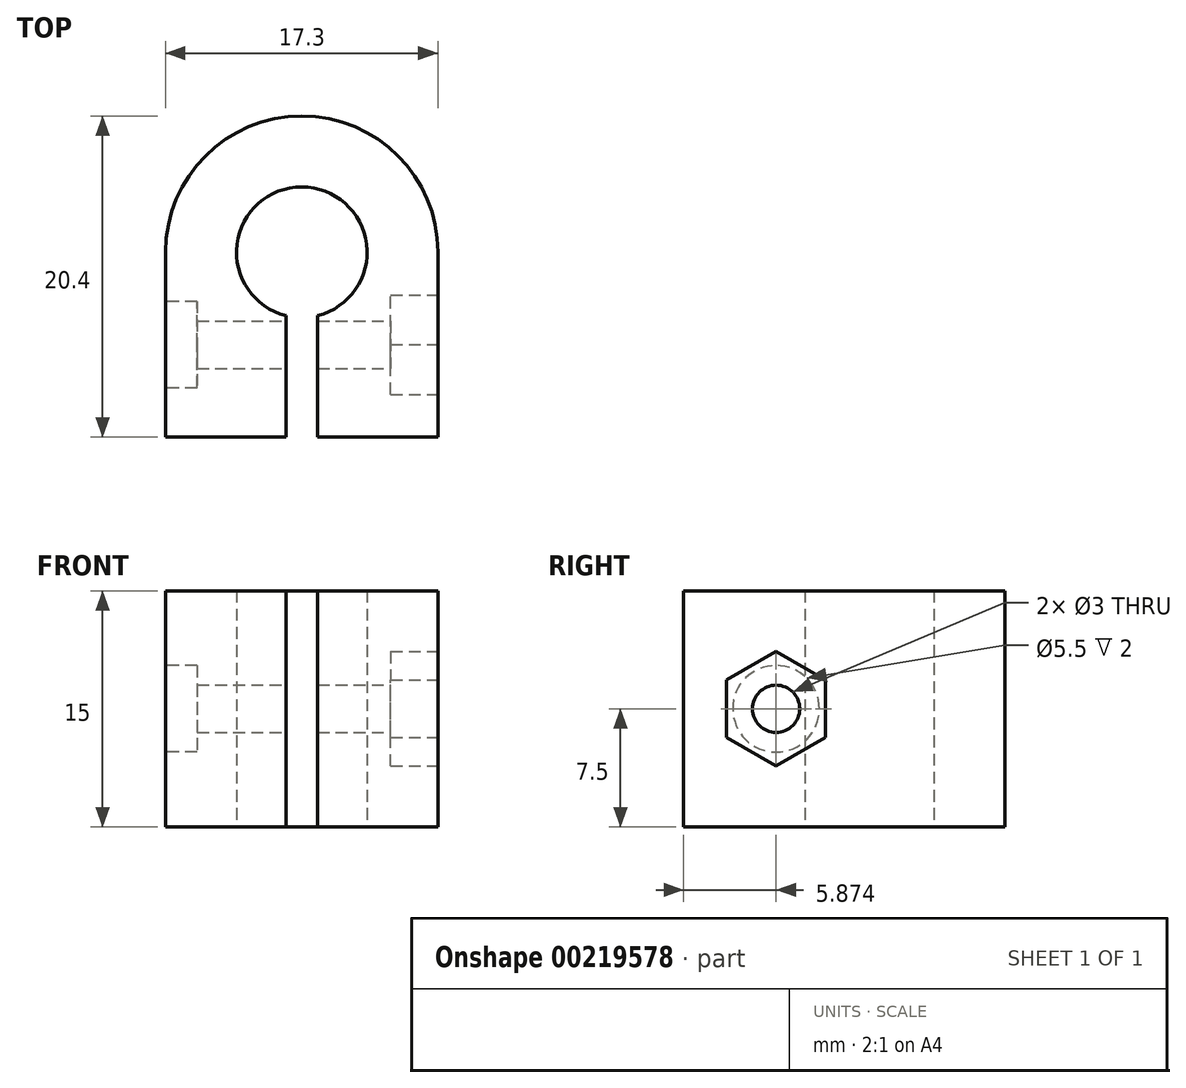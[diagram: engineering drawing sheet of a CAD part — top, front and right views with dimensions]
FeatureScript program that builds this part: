
annotation { "Feature Type Name" : "Feature", "Feature Type Description" : "" }
export const myFeature = defineFeature(function(context is Context, id is Id, definition is map)
    precondition{}
    {
        {
            var Q0;
            Q0=qCreatedBy(makeId("Top.planeOp"),FACE);
            var sketch = newSketch(context, id + "F0", { "sketchPlane" : qUnion([Q0])});
            skCircle(sketch, "E0", {"center": v(0, 0) * mm, "radius": 4.15 * mm});
            skCircle(sketch, "E1", {"center": v(0, 0) * mm, "radius": 8.65 * mm});
            skLineSegment(sketch, "E2.bottom", {"start": v(-8.65, -11.75) * mm, "end": v(8.65, -11.75) * mm});
            skLineSegment(sketch, "E2.top", {"start": v(-8.65, 0) * mm, "end": v(8.65, 0) * mm});
            skLineSegment(sketch, "E2.left", {"start": v(-8.65, -11.75) * mm, "end": v(-8.65, 0) * mm});
            skLineSegment(sketch, "E2.right", {"start": v(8.65, -11.75) * mm, "end": v(8.65, 0) * mm});
            skLineSegment(sketch, "E3.bottom", {"start": v(1, -4.03) * mm, "end": v(-1, -4.03) * mm});
            skLineSegment(sketch, "E3.top", {"start": v(1, -11.75) * mm, "end": v(-1, -11.75) * mm});
            skLineSegment(sketch, "E3.left", {"start": v(1, -4.03) * mm, "end": v(1, -11.75) * mm});
            skLineSegment(sketch, "E3.right", {"start": v(-1, -4.03) * mm, "end": v(-1, -11.75) * mm});
            skPoint(sketch, "E3.middle", {"position": v(0, -7.89) * mm});
            skSolve(sketch);
        }
        {
            var Q0;
            {var subQ0=sQuery(id+"F0.wireOp",EDGE,"E2.left");Q0=makeQuery(id+"F0.imprint","IMPRINT",FACE,{"disambiguationData":[TD([[makeQuery(id+"F0.imprint","IMPRINT",EDGE,{"derivedFrom":subQ0}),-1.0]])]});}
            var Q1;
            {var subQ0=sQuery(id+"F0.wireOp",EDGE,"E2.right");Q1=makeQuery(id+"F0.imprint","IMPRINT",FACE,{"disambiguationData":[TD([[makeQuery(id+"F0.imprint","IMPRINT",EDGE,{"derivedFrom":subQ0}),1.0]])]});}
            var Q2;
            {var subQ0=sQuery(id+"F0.wireOp",EDGE,"E2.top");var subQ1=sQuery(id+"F0.wireOp",EDGE,"E0");var subQ2=makeQuery(id+"F0.imprint","INTERSECT",VERTEX,{"disambiguationData":[OD(0.0)],"derivedFrom":[subQ1,subQ0]});Q2=makeQuery(id+"F0.imprint","IMPRINT",FACE,{"disambiguationData":[TD([[makeQuery(id+"F0.imprint","IMPRINT",EDGE,{"disambiguationData":[TD([[subQ2,1.0]])],"derivedFrom":subQ1}),-1.0]])]});}
            var Q3;
            {var subQ1=sQuery(id+"F0.wireOp",EDGE,"E0");var subQ3=sQuery(id+"F0.wireOp",EDGE,"E2.top");var subQ4=makeQuery(id+"F0.imprint","INTERSECT",VERTEX,{"disambiguationData":[OD(0.0)],"derivedFrom":[subQ1,subQ3]});Q3=makeQuery(id+"F0.imprint","IMPRINT",FACE,{"disambiguationData":[TD([[makeQuery(id+"F0.imprint","IMPRINT",EDGE,{"disambiguationData":[TD([[subQ4,-1.0]])],"derivedFrom":subQ1}),-1.0]])]});}
            var Q4;
            {var subQ1=sQuery(id+"F0.wireOp",EDGE,"E0");var subQ3=sQuery(id+"F0.wireOp",EDGE,"E2.top");var subQ4=makeQuery(id+"F0.imprint","INTERSECT",VERTEX,{"disambiguationData":[OD(1.0)],"derivedFrom":[subQ1,subQ3]});Q4=makeQuery(id+"F0.imprint","IMPRINT",FACE,{"disambiguationData":[TD([[makeQuery(id+"F0.imprint","IMPRINT",EDGE,{"disambiguationData":[TD([[subQ4,1.0]])],"derivedFrom":subQ1}),-1.0]])]});}
            extrude(context, id + "F1", {"entities" : qUnion([Q0, Q1, Q2, Q3, Q4]), "depth" : 15 * mm});
        }
        {
            var Q0;
            Q0=makeQuery(id+"F1.opExtrude","SWEPT_FACE",FACE,{"disambiguationData":[OSD([sQuery(id+"F0.wireOp",EDGE,"E2.right")])]});
            var sketch = newSketch(context, id + "F2", { "sketchPlane" : qUnion([Q0])});
            skCircle(sketch, "E4", {"center": v(-5.88, 7.5) * mm, "radius": 1.5 * mm});
            skPoint(sketch, "E4.centerSnap0", {"position": v(0, 7.5) * mm});
            skPoint(sketch, "E4.centerSnap1", {"position": v(-5.88, 15) * mm});
            skSolve(sketch);
        }
        {
            var Q0;
            Q0 = qSketchRegion(id + "F2", true);
            extrude(context, id + "F3", {"entities" : qUnion([Q0]), "operationType" : NewBodyOperationType.REMOVE, "endBound" : BoundingType.THROUGH_ALL, "oppositeDirection" : true, "depth" : 25 * mm});
        }
        {
            var Q0;
            Q0=makeQuery(id+"F1.opExtrude","SWEPT_FACE",FACE,{"disambiguationData":[OSD([sQuery(id+"F0.wireOp",EDGE,"E2.right")])]});
            var sketch = newSketch(context, id + "F4", { "sketchPlane" : qUnion([Q0])});
            skCircle(sketch, "E5.cCircle", {"center": v(-5.88, 7.5) * mm, "radius": 3.15 * mm, "construction": true});
            skLineSegment(sketch, "E5.0", {"start": v(-5.88, 11.14) * mm, "end": v(-2.73, 9.32) * mm});
            skLineSegment(sketch, "E5.1", {"start": v(-2.73, 9.32) * mm, "end": v(-2.73, 5.68) * mm});
            skLineSegment(sketch, "E5.2", {"start": v(-2.73, 5.68) * mm, "end": v(-5.88, 3.86) * mm});
            skLineSegment(sketch, "E5.3", {"start": v(-5.88, 3.86) * mm, "end": v(-9.03, 5.68) * mm});
            skLineSegment(sketch, "E5.4", {"start": v(-9.03, 5.68) * mm, "end": v(-9.03, 9.32) * mm});
            skLineSegment(sketch, "E5.5", {"start": v(-9.03, 9.32) * mm, "end": v(-5.88, 11.14) * mm});
            skPoint(sketch, "E5.0.midPoint", {"position": v(-4.3, 10.23) * mm});
            skSolve(sketch);
        }
        {
            var Q0;
            Q0 = qSketchRegion(id + "F4", true);
            extrude(context, id + "F5", {"entities" : qUnion([Q0]), "operationType" : NewBodyOperationType.REMOVE, "oppositeDirection" : true, "depth" : 3 * mm});
        }
        {
            var Q0;
            Q0=makeQuery(id+"F1.opExtrude","SWEPT_FACE",FACE,{"disambiguationData":[OSD([sQuery(id+"F0.wireOp",EDGE,"E2.left")])]});
            var sketch = newSketch(context, id + "F6", { "sketchPlane" : qUnion([Q0])});
            skCircle(sketch, "E6", {"center": v(5.88, 7.5) * mm, "radius": 2.75 * mm});
            skSolve(sketch);
        }
        {
            var Q0;
            Q0 = qSketchRegion(id + "F6", true);
            extrude(context, id + "F7", {"entities" : qUnion([Q0]), "operationType" : NewBodyOperationType.REMOVE, "oppositeDirection" : true, "depth" : 2 * mm});
        }
    });
